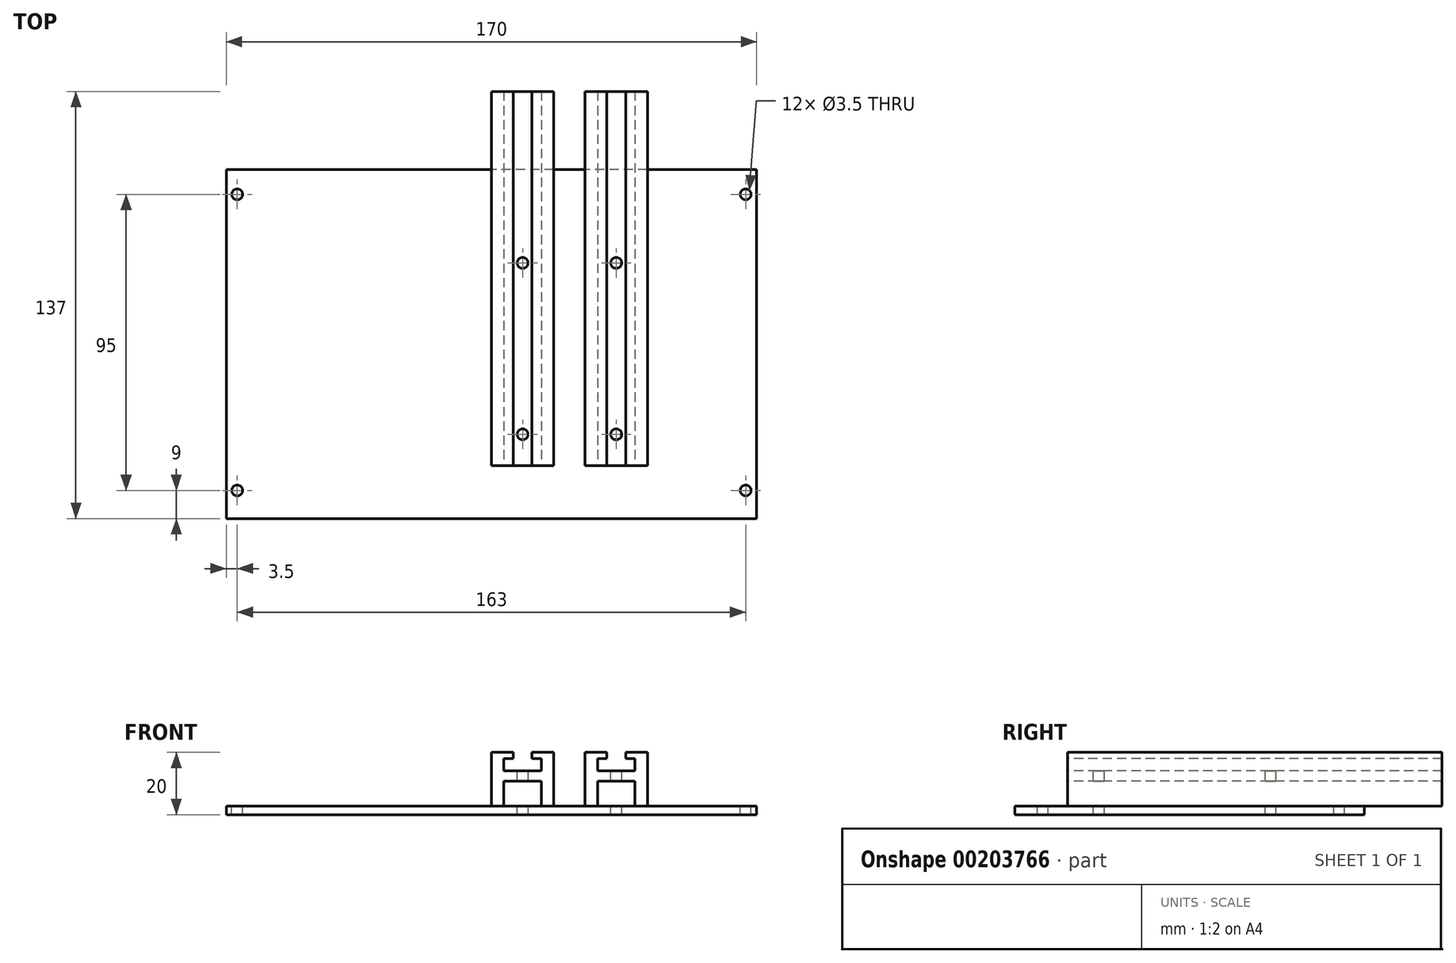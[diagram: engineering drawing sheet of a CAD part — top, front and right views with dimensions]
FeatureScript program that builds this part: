
annotation { "Feature Type Name" : "Feature", "Feature Type Description" : "" }
export const myFeature = defineFeature(function(context is Context, id is Id, definition is map)
    precondition{}
    {
        {
            var Q0;
            Q0=qCreatedBy(makeId("Top.planeOp"),FACE);
            var sketch = newSketch(context, id + "F0", { "sketchPlane" : qUnion([Q0])});
            skLineSegment(sketch, "E0.bottom", {"start": v(85, -56) * mm, "end": v(-85, -56) * mm});
            skLineSegment(sketch, "E0.top", {"start": v(85, 56) * mm, "end": v(-85, 56) * mm});
            skLineSegment(sketch, "E0.left", {"start": v(85, -56) * mm, "end": v(85, 56) * mm});
            skLineSegment(sketch, "E0.right", {"start": v(-85, -56) * mm, "end": v(-85, 56) * mm});
            skPoint(sketch, "E0.middle", {"position": v(0, 0) * mm});
            skSolve(sketch);
        }
        {
            var Q0;
            Q0=makeQuery(id+"F0.imprint","IMPRINT",FACE,{"disambiguationData":[TD([[makeQuery(id+"F0.imprint","IMPRINT",EDGE,{"derivedFrom":sQuery(id+"F0.wireOp",EDGE,"E0.bottom")}),-1.0]])]});
            extrude(context, id + "F1", {"entities" : qUnion([Q0]), "oppositeDirection" : true, "depth" : 2.75 * mm, "offsetDistance" : 25 * mm});
        }
        {
            var Q0;
            Q0=makeQuery(id+"F1.opExtrude","CAP_FACE",FACE,{"disambiguationData":[OSD([sQuery(id+"F0.wireOp",EDGE,"E0.bottom"),sQuery(id+"F0.wireOp",EDGE,"E0.top"),sQuery(id+"F0.wireOp",EDGE,"E0.left"),sQuery(id+"F0.wireOp",EDGE,"E0.right")])],"isStart":true});
            var sketch = newSketch(context, id + "F2", { "sketchPlane" : qUnion([Q0])});
            skLineSegment(sketch, "E1", {"start": v(-85, -56) * mm, "end": v(-81.5, -56) * mm, "construction": true});
            skLineSegment(sketch, "E2", {"start": v(-81.5, -56) * mm, "end": v(-81.5, -47) * mm, "construction": true});
            skCircle(sketch, "E3", {"center": v(-81.5, -47) * mm, "radius": 1.75 * mm});
            skCircle(sketch, "E4.0.1.0", {"center": v(-81.5, 48) * mm, "radius": 1.75 * mm});
            skCircle(sketch, "E4.1.0.0", {"center": v(81.5, -47) * mm, "radius": 1.75 * mm});
            skCircle(sketch, "E4.1.1.0", {"center": v(81.5, 48) * mm, "radius": 1.75 * mm});
            skLineSegment(sketch, "E4.direction1", {"start": v(-81.5, -47) * mm, "end": v(81.5, -47) * mm, "construction": true});
            skLineSegment(sketch, "E4.direction2", {"start": v(-81.5, -47) * mm, "end": v(-81.5, 48) * mm, "construction": true});
            skSolve(sketch);
        }
        {
            var Q0;
            Q0=makeQuery(id+"F2.imprint","IMPRINT",FACE,{"disambiguationData":[TD([[makeQuery(id+"F2.imprint","IMPRINT",EDGE,{"derivedFrom":sQuery(id+"F2.wireOp",EDGE,"E4.0.1.0")}),1.0]])]});
            var Q1;
            Q1=makeQuery(id+"F2.imprint","IMPRINT",FACE,{"disambiguationData":[TD([[makeQuery(id+"F2.imprint","IMPRINT",EDGE,{"derivedFrom":sQuery(id+"F2.wireOp",EDGE,"E3")}),1.0]])]});
            var Q2;
            Q2=makeQuery(id+"F2.imprint","IMPRINT",FACE,{"disambiguationData":[TD([[makeQuery(id+"F2.imprint","IMPRINT",EDGE,{"derivedFrom":sQuery(id+"F2.wireOp",EDGE,"E4.1.1.0")}),1.0]])]});
            var Q3;
            Q3=makeQuery(id+"F2.imprint","IMPRINT",FACE,{"disambiguationData":[TD([[makeQuery(id+"F2.imprint","IMPRINT",EDGE,{"derivedFrom":sQuery(id+"F2.wireOp",EDGE,"E4.1.0.0")}),1.0]])]});
            extrude(context, id + "F3", {"entities" : qUnion([Q0, Q1, Q2, Q3]), "operationType" : NewBodyOperationType.REMOVE, "endBound" : BoundingType.UP_TO_NEXT, "oppositeDirection" : true, "depth" : 25 * mm, "offsetDistance" : 25 * mm});
        }
        {
            var Q0;
            Q0=makeQuery(id+"F1.opExtrude","SWEPT_FACE",FACE,{"disambiguationData":[OSD([sQuery(id+"F0.wireOp",EDGE,"E0.top")])]});
            var sketch = newSketch(context, id + "F4", { "sketchPlane" : qUnion([Q0])});
            skLineSegment(sketch, "E5", {"start": v(-85, -2.75) * mm, "end": v(-50, -2.75) * mm, "construction": true});
            skLineSegment(sketch, "E6", {"start": v(-50, -2.75) * mm, "end": v(-50, 17.25) * mm});
            skLineSegment(sketch, "E7", {"start": v(-50, 17.25) * mm, "end": v(-43, 17.25) * mm});
            skLineSegment(sketch, "E8", {"start": v(-43, 17.25) * mm, "end": v(-43, 15.25) * mm});
            skLineSegment(sketch, "E9", {"start": v(-43, 15.25) * mm, "end": v(-46, 15.25) * mm});
            skLineSegment(sketch, "E10", {"start": v(-46, 15.25) * mm, "end": v(-46, 11.25) * mm});
            skLineSegment(sketch, "E11", {"start": v(-46, 11.25) * mm, "end": v(-34, 11.25) * mm});
            skLineSegment(sketch, "E12", {"start": v(-50, 17.25) * mm, "end": v(-40, 17.25) * mm, "construction": true});
            skLineSegment(sketch, "E13", {"start": v(-40, 17.25) * mm, "end": v(-40, -15.6) * mm, "construction": true});
            skLineSegment(sketch, "E14.MirrorCS", {"start": v(-34, 15.25) * mm, "end": v(-34, 11.25) * mm});
            skLineSegment(sketch, "E15.MirrorCS", {"start": v(-37, 17.25) * mm, "end": v(-37, 15.25) * mm});
            skLineSegment(sketch, "E16.MirrorCS", {"start": v(-37, 15.25) * mm, "end": v(-34, 15.25) * mm});
            skLineSegment(sketch, "E17.MirrorCS", {"start": v(-30, 17.25) * mm, "end": v(-37, 17.25) * mm});
            skLineSegment(sketch, "E18.MirrorCS", {"start": v(-30, 17.25) * mm, "end": v(-40, 17.25) * mm, "construction": true});
            skLineSegment(sketch, "E19.MirrorCS", {"start": v(-30, -2.75) * mm, "end": v(-30, 17.25) * mm});
            skLineSegment(sketch, "E20", {"start": v(-50, -2.75) * mm, "end": v(-30, -2.75) * mm});
            skLineSegment(sketch, "E21", {"start": v(-46, 11.25) * mm, "end": v(-46, 0) * mm, "construction": true});
            skLineSegment(sketch, "E22", {"start": v(-46, 0) * mm, "end": v(-34, 0) * mm});
            skLineSegment(sketch, "E23", {"start": v(-34, 11.25) * mm, "end": v(-34, -7.77) * mm, "construction": true});
            skLineSegment(sketch, "E24", {"start": v(-34, 0) * mm, "end": v(-34, 8) * mm});
            skLineSegment(sketch, "E25", {"start": v(-34, 8) * mm, "end": v(-46, 8) * mm});
            skLineSegment(sketch, "E26", {"start": v(-46, 8) * mm, "end": v(-46, 0) * mm});
            skLineSegment(sketch, "E27", {"start": v(-40, -15.6) * mm, "end": v(-25, -15.6) * mm, "construction": true});
            skLineSegment(sketch, "E28", {"start": v(-25, -15.6) * mm, "end": v(-25, 45.43) * mm, "construction": true});
            skLineSegment(sketch, "E29.MirrorCS", {"start": v(-13, 17.25) * mm, "end": v(-13, 15.25) * mm});
            skLineSegment(sketch, "E30.MirrorCS", {"start": v(-13, 15.25) * mm, "end": v(-16, 15.25) * mm});
            skLineSegment(sketch, "E31.MirrorCS", {"start": v(-20, 17.25) * mm, "end": v(-10, 17.25) * mm, "construction": true});
            skLineSegment(sketch, "E32.MirrorCS", {"start": v(-20, 17.25) * mm, "end": v(-13, 17.25) * mm});
            skLineSegment(sketch, "E33.MirrorCS", {"start": v(-7, 17.25) * mm, "end": v(-7, 15.25) * mm});
            skLineSegment(sketch, "E34.MirrorCS", {"start": v(0, 17.25) * mm, "end": v(-7, 17.25) * mm});
            skLineSegment(sketch, "E35.MirrorCS", {"start": v(-4, 8) * mm, "end": v(-4, 0) * mm});
            skLineSegment(sketch, "E36.MirrorCS", {"start": v(-16, 15.25) * mm, "end": v(-16, 11.25) * mm});
            skLineSegment(sketch, "E37.MirrorCS", {"start": v(0, 17.25) * mm, "end": v(-10, 17.25) * mm, "construction": true});
            skLineSegment(sketch, "E38.MirrorCS", {"start": v(-4, 15.25) * mm, "end": v(-4, 11.25) * mm});
            skLineSegment(sketch, "E39.MirrorCS", {"start": v(-7, 15.25) * mm, "end": v(-4, 15.25) * mm});
            skLineSegment(sketch, "E40.MirrorCS", {"start": v(-16, 0) * mm, "end": v(-16, 8) * mm});
            skLineSegment(sketch, "E41.MirrorCS", {"start": v(-4, 11.25) * mm, "end": v(-4, 0) * mm, "construction": true});
            skLineSegment(sketch, "E42.MirrorCS", {"start": v(-4, 0) * mm, "end": v(-16, 0) * mm});
            skLineSegment(sketch, "E43.MirrorCS", {"start": v(-4, 11.25) * mm, "end": v(-16, 11.25) * mm});
            skLineSegment(sketch, "E44.MirrorCS", {"start": v(-16, 11.25) * mm, "end": v(-16, -7.77) * mm, "construction": true});
            skLineSegment(sketch, "E45.MirrorCS", {"start": v(-16, 8) * mm, "end": v(-4, 8) * mm});
            skLineSegment(sketch, "E46.MirrorCS", {"start": v(-20, -2.75) * mm, "end": v(-20, 17.25) * mm});
            skLineSegment(sketch, "E47.MirrorCS", {"start": v(0, -2.75) * mm, "end": v(-20, -2.75) * mm});
            skLineSegment(sketch, "E48.MirrorCS", {"start": v(0, -2.75) * mm, "end": v(0, 17.25) * mm});
            skSolve(sketch);
        }
        {
            var Q0;
            {var subQ1=sQuery(id+"F4.wireOp",EDGE,"E7");Q0=makeQuery(id+"F4.imprint","IMPRINT",FACE,{"disambiguationData":[TD([[makeQuery(id+"F4.imprint","IMPRINT",EDGE,{"derivedFrom":subQ1}),-1.0]])]});}
            var Q1;
            Q1=makeQuery(id+"F4.imprint","IMPRINT",FACE,{"disambiguationData":[TD([[makeQuery(id+"F4.imprint","IMPRINT",EDGE,{"derivedFrom":sQuery(id+"F4.wireOp",EDGE,"E29.MirrorCS")}),-1.0]])]});
            extrude(context, id + "F5", {"entities" : qUnion([Q0, Q1]), "depth" : 40 * mm, "offsetDistance" : 25 * mm, "hasSecondDirection" : true, "secondDirectionOppositeDirection" : true, "secondDirectionDepth" : 80 * mm});
        }
        {
            var Q0;
            Q0=makeQuery(id+"F5.opExtrude","SWEPT_FACE",FACE,{"disambiguationData":[OSD([sQuery(id+"F4.wireOp",EDGE,"E43.MirrorCS")])]});
            var sketch = newSketch(context, id + "F6", { "sketchPlane" : qUnion([Q0])});
            skLineSegment(sketch, "E49", {"start": v(10, -29) * mm, "end": v(10, -24) * mm, "construction": true});
            skCircle(sketch, "E50", {"center": v(10, -29) * mm, "radius": 1.75 * mm});
            skCircle(sketch, "E51.0.1.0", {"center": v(10, 26) * mm, "radius": 1.75 * mm});
            skCircle(sketch, "E51.1.0.0", {"center": v(40, -29) * mm, "radius": 1.75 * mm});
            skCircle(sketch, "E51.1.1.0", {"center": v(40, 26) * mm, "radius": 1.75 * mm});
            skLineSegment(sketch, "E51.direction1", {"start": v(10, -29) * mm, "end": v(40, -29) * mm, "construction": true});
            skLineSegment(sketch, "E51.direction2", {"start": v(10, -29) * mm, "end": v(10, 26) * mm, "construction": true});
            skSolve(sketch);
        }
        {
            var Q0;
            Q0=makeQuery(id+"F5.opExtrude","SWEPT_BODY",BODY,{"disambiguationData":[OSD([sQuery(id+"F0.wireOp",EDGE,"E0.top"),sQuery(id+"F4.wireOp",EDGE,"E6"),sQuery(id+"F4.wireOp",EDGE,"E7"),sQuery(id+"F4.wireOp",EDGE,"E8"),sQuery(id+"F4.wireOp",EDGE,"E9"),sQuery(id+"F4.wireOp",EDGE,"E10"),sQuery(id+"F4.wireOp",EDGE,"E11"),sQuery(id+"F4.wireOp",EDGE,"E14.MirrorCS"),sQuery(id+"F4.wireOp",EDGE,"E15.MirrorCS"),sQuery(id+"F4.wireOp",EDGE,"E16.MirrorCS"),sQuery(id+"F4.wireOp",EDGE,"E17.MirrorCS"),sQuery(id+"F4.wireOp",EDGE,"E19.MirrorCS"),sQuery(id+"F4.wireOp",EDGE,"E24"),sQuery(id+"F4.wireOp",EDGE,"E25"),sQuery(id+"F4.wireOp",EDGE,"E26")])]});
            var Q1;
            Q1=makeQuery(id+"F5.opExtrude","SWEPT_BODY",BODY,{"disambiguationData":[OSD([sQuery(id+"F0.wireOp",EDGE,"E0.top"),sQuery(id+"F4.wireOp",EDGE,"E29.MirrorCS"),sQuery(id+"F4.wireOp",EDGE,"E30.MirrorCS"),sQuery(id+"F4.wireOp",EDGE,"E32.MirrorCS"),sQuery(id+"F4.wireOp",EDGE,"E33.MirrorCS"),sQuery(id+"F4.wireOp",EDGE,"E34.MirrorCS"),sQuery(id+"F4.wireOp",EDGE,"E35.MirrorCS"),sQuery(id+"F4.wireOp",EDGE,"E36.MirrorCS"),sQuery(id+"F4.wireOp",EDGE,"E38.MirrorCS"),sQuery(id+"F4.wireOp",EDGE,"E39.MirrorCS"),sQuery(id+"F4.wireOp",EDGE,"E40.MirrorCS"),sQuery(id+"F4.wireOp",EDGE,"E43.MirrorCS"),sQuery(id+"F4.wireOp",EDGE,"E45.MirrorCS"),sQuery(id+"F4.wireOp",EDGE,"E46.MirrorCS"),sQuery(id+"F4.wireOp",EDGE,"E48.MirrorCS")])]});
            transform(context, id + "F7", {"entities" : qUnion([Q0, Q1]), "transformType" : TransformType.TRANSLATION_3D, "dx" : 0 * mm, "dy" : -15 * mm, "dz" : 0 * mm, "makeCopy" : false});
        }
        {
            var Q0;
            Q0=makeQuery(id+"F6.imprint","IMPRINT",FACE,{"disambiguationData":[TD([[makeQuery(id+"F6.imprint","IMPRINT",EDGE,{"derivedFrom":sQuery(id+"F6.wireOp",EDGE,"E50")}),1.0]])]});
            var Q1;
            Q1=makeQuery(id+"F6.imprint","IMPRINT",FACE,{"disambiguationData":[TD([[makeQuery(id+"F6.imprint","IMPRINT",EDGE,{"derivedFrom":sQuery(id+"F6.wireOp",EDGE,"E51.1.0.0")}),1.0]])]});
            var Q2;
            Q2=makeQuery(id+"F6.imprint","IMPRINT",FACE,{"disambiguationData":[TD([[makeQuery(id+"F6.imprint","IMPRINT",EDGE,{"derivedFrom":sQuery(id+"F6.wireOp",EDGE,"E51.1.1.0")}),1.0]])]});
            var Q3;
            Q3=makeQuery(id+"F6.imprint","IMPRINT",FACE,{"disambiguationData":[TD([[makeQuery(id+"F6.imprint","IMPRINT",EDGE,{"derivedFrom":sQuery(id+"F6.wireOp",EDGE,"E51.0.1.0")}),1.0]])]});
            extrude(context, id + "F8", {"entities" : qUnion([Q0, Q1, Q2, Q3]), "operationType" : NewBodyOperationType.REMOVE, "endBound" : BoundingType.THROUGH_ALL, "oppositeDirection" : true, "depth" : 25 * mm, "offsetDistance" : 25 * mm});
        }
    });
